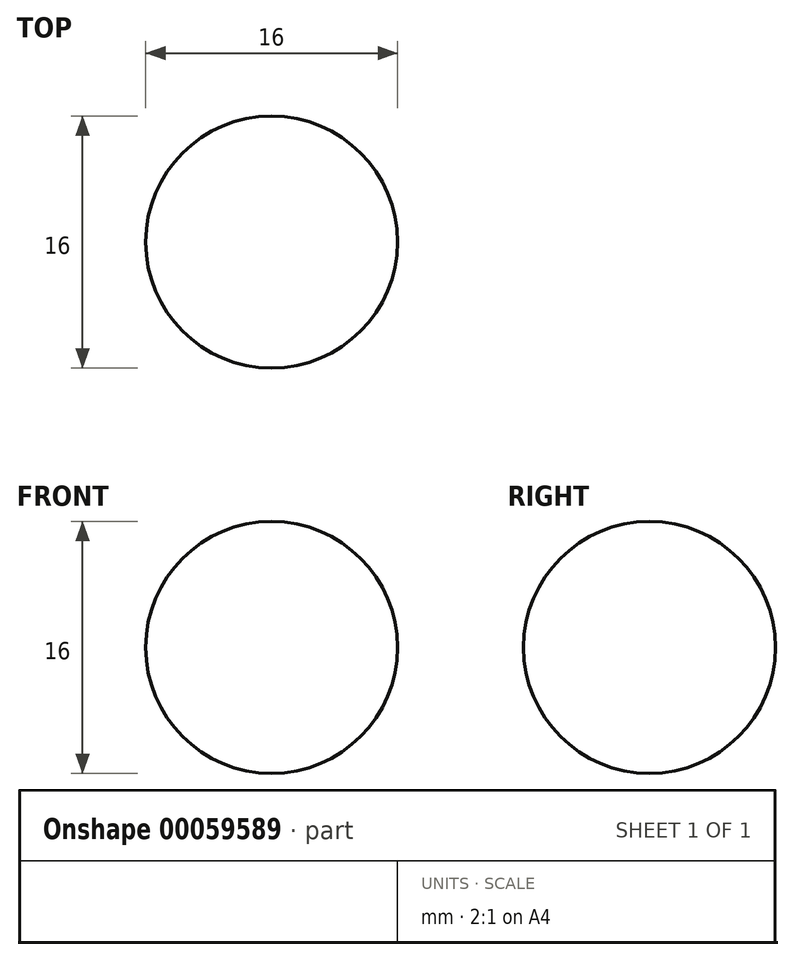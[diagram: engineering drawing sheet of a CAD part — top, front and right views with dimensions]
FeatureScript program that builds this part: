
annotation { "Feature Type Name" : "Feature", "Feature Type Description" : "" }
export const myFeature = defineFeature(function(context is Context, id is Id, definition is map)
    precondition{}
    {
        {
            var Q0;
            Q0=qCreatedBy(makeId("Front.planeOp"),FACE);
            var sketch = newSketch(context, id + "F0", { "sketchPlane" : qUnion([Q0])});
            skArc(sketch, "E0", {"start": v(0, -8) * mm, "mid": v(8, 0) * mm, "end": v(0, 8) * mm});
            skLineSegment(sketch, "E1", {"start": v(0, 8) * mm, "end": v(0, -8) * mm});
            skSolve(sketch);
        }
        {
            var Q0;
            Q0=makeQuery(id+"F0.imprint","IMPRINT",FACE,{"disambiguationData":[TD([[makeQuery(id+"F0.imprint","IMPRINT",EDGE,{"derivedFrom":sQuery(id+"F0.wireOp",EDGE,"E0")}),1.0]])]});
            var Q1;
            Q1=sQuery(id+"F0.wireOp",EDGE,"E1");
            revolve(context, id + "F1", {"entities" : qUnion([Q0]), "axis" : qUnion([Q1]), "revolveType" : RevolveType.FULL});
        }
    });
